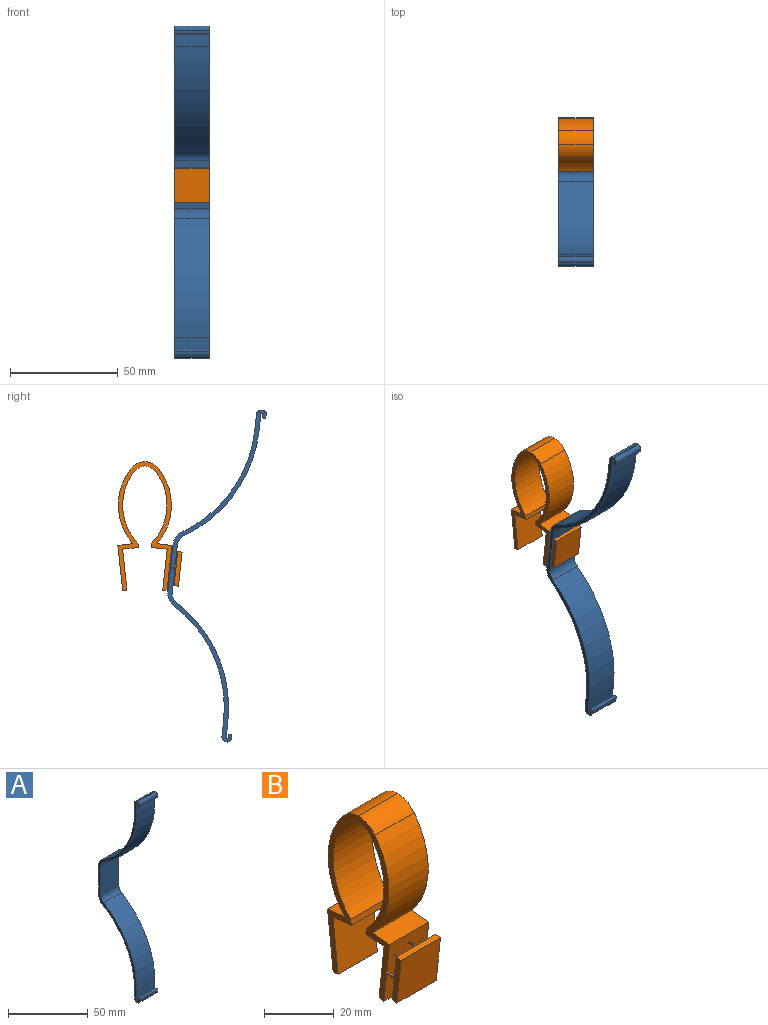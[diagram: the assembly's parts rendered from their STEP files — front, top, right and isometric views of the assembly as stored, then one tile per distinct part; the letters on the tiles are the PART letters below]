
ASSEMBLY  parts=2 mates=3
PART A: 31 faces, bbox 15.9x36.5x154.6 mm
  f0: plane 15.88x1.08mm, normal (0,1,0), area 17.2mm2, adj f9,f10,f15,f16
  f1: plane 15.88x7.55mm, normal (0,-1,0), area 119.8mm2, adj f2,f9,f10,f16
  f2: cylinder r=61.15mm len=52.35mm, axis (-1,0,0), area 997.7mm2, adj f1,f9,f10,f11
  f3: plane 22.18x15.88mm, normal (0,-1,0), area 349.4mm2, adj f9,f10,f11,f24,f30
  f4: plane 22.18x15.88mm, normal (0,1,0), area 349.3mm2, adj f9,f10,f14,f27,f30
  f5: cylinder r=59.15mm len=50.64mm, axis (-1,0,0), area 965mm2, adj f6,f9,f10,f14
  f6: plane 15.88x7.24mm, normal (0,1,0), area 114.9mm2, adj f5,f9,f10,f13
  f7: plane 15.88x0.39mm, normal (0,0,1), area 6.1mm2, adj f9,f10,f12,f13
  f8: plane 15.88x1.28mm, normal (0,-1,0), area 20.4mm2, adj f9,f10,f12,f15
  f9: plane 154.64x36.46mm, normal (1,0,0), area 365.1mm2, adj f0,f1,f2,f3,f4,f5,f6,f7
  f10: plane 154.64x36.46mm, normal (-1,0,0), area 365.1mm2, adj f0,f1,f2,f3,f4,f5,f6,f7
  f11: cylinder r=5.08mm len=15.88mm, axis (-1,0,0), area 82.9mm2, adj f2,f3,f9,f10
  f12: cylinder r=1.78mm len=15.88mm, axis (-1,0,0), area 44.3mm2, adj f7,f8,f9,f10
  f13: cylinder r=2.29mm len=15.88mm, axis (-1,0,0), area 57mm2, adj f6,f7,f9,f10
  f14: cylinder r=7.09mm len=15.88mm, axis (-1,0,0), area 115.6mm2, adj f4,f5,f9,f10
  f15: cylinder r=0.75mm len=15.88mm, axis (-1,0,0), area 37.4mm2, adj f0,f8,f9,f10
  f16: cylinder r=0.48mm len=15.88mm, axis (-1,0,0), area 23.8mm2, adj f0,f1,f9,f10
  f17: plane 15.88x1.08mm, normal (0,1,0), area 17.2mm2, adj f9,f10,f28,f29
  f18: plane 15.88x7.55mm, normal (0,-1,0), area 119.8mm2, adj f9,f10,f19,f29
  f19: cylinder r=61.15mm len=52.35mm, axis (-1,0,0), area 997.7mm2, adj f9,f10,f18,f24
  f20: cylinder r=59.15mm len=50.64mm, axis (-1,0,0), area 965mm2, adj f9,f10,f21,f27
  f21: plane 15.88x7.24mm, normal (0,1,0), area 114.9mm2, adj f9,f10,f20,f26
  f22: plane 15.88x0.39mm, normal (0,0,-1), area 6.1mm2, adj f9,f10,f25,f26
  f23: plane 15.88x1.28mm, normal (0,-1,0), area 20.4mm2, adj f9,f10,f25,f28
  f24: cylinder r=5.08mm len=15.88mm, axis (-1,0,0), area 82.9mm2, adj f3,f9,f10,f19
  f25: cylinder r=1.78mm len=15.88mm, axis (-1,0,0), area 44.3mm2, adj f9,f10,f22,f23
  f26: cylinder r=2.29mm len=15.88mm, axis (-1,0,0), area 57mm2, adj f9,f10,f21,f22
  f27: cylinder r=7.09mm len=15.88mm, axis (-1,0,0), area 115.6mm2, adj f4,f9,f10,f20
  f28: cylinder r=0.75mm len=15.88mm, axis (-1,0,0), area 37.4mm2, adj f9,f10,f17,f23
  f29: cylinder r=0.48mm len=15.88mm, axis (-1,0,0), area 23.8mm2, adj f9,f10,f17,f18
  f30: cylinder r=0.94mm len=2mm, axis (0,1,0), area 11.8mm2, adj f3,f4
PART B: 55 faces, bbox 15.9x29.7x59.8 mm
  f0: plane 15.88x15.78mm, normal (0,0.99,0.11), area 232.3mm2, adj f3,f5,f23,f24,f25,f27,f28,f29
  f1: plane 20.93x15.88mm, normal (0,-0.99,-0.11), area 314.4mm2, adj f2,f3,f5,f8,f23,f24,f25,f27
  f2: plane 15.88x1.99mm, normal (0,0.11,-0.99), area 31.8mm2, adj f1,f3,f5,f16
  f3: plane 59.8x29.74mm, normal (1,0,0), area 321.2mm2, adj f0,f1,f2,f4,f6,f7,f8,f9
  f4: plane 15.88x1.99mm, normal (0,-0.11,-0.99), area 31.8mm2, adj f3,f5,f11,f21
  f5: plane 59.8x29.74mm, normal (-1,0,0), area 321.2mm2, adj f0,f1,f2,f4,f6,f7,f8,f9
  f6: plane 15.88x6.88mm, normal (0,0.11,0.99), area 109.8mm2, adj f3,f5,f7,f11
  f7: cylinder r=27.38mm len=34.62mm, axis (1,0,0), area 595.2mm2, adj f3,f5,f6,f12
  f8: plane 15.88x6.88mm, normal (0,-0.11,0.99), area 109.8mm2, adj f1,f3,f5,f9
  f9: cylinder r=27.38mm len=34.62mm, axis (1,0,0), area 595.2mm2, adj f3,f5,f8,f10
  f10: cylinder r=9.08mm len=15.88mm, axis (1,0,0), area 122.1mm2, adj f3,f5,f9,f12
  f11: plane 20.93x15.88mm, normal (0,0.99,-0.11), area 334.2mm2, adj f3,f4,f5,f6
  f12: cylinder r=9.08mm len=15.88mm, axis (1,0,0), area 122.1mm2, adj f3,f5,f7,f10
  f13: cylinder r=25.38mm len=33.13mm, axis (1,0,0), area 574.1mm2, adj f3,f5,f14,f17
  f14: plane 15.88x1.99mm, normal (0,0.99,0.11), area 31.8mm2, adj f3,f5,f13,f15
  f15: plane 15.88x7.36mm, normal (0,0.11,-0.99), area 117.5mm2, adj f3,f5,f14,f16
  f16: plane 18.94x15.88mm, normal (0,0.99,0.11), area 302.4mm2, adj f2,f3,f5,f15
  f17: cylinder r=7.08mm len=15.88mm, axis (1,0,0), area 93.1mm2, adj f3,f5,f13,f22
  f18: cylinder r=25.38mm len=33.13mm, axis (1,0,0), area 574.1mm2, adj f3,f5,f19,f22
  f19: plane 15.88x1.99mm, normal (0,-0.99,0.11), area 31.8mm2, adj f3,f5,f18,f20
  f20: plane 15.88x7.36mm, normal (0,-0.11,-0.99), area 117.5mm2, adj f3,f5,f19,f21
  f21: plane 18.94x15.88mm, normal (0,-0.99,0.11), area 302.4mm2, adj f3,f4,f5,f20
  f22: cylinder r=7.08mm len=15.88mm, axis (1,0,0), area 93.1mm2, adj f3,f5,f17,f18
  f23: cylinder r=2.38mm len=5.06mm, axis (0,0.99,0.11), area 44.9mm2, adj f0,f1
  f24: plane 15.88x4.97mm, normal (0,-0.11,0.99), area 32.9mm2, adj f0,f1,f3,f5,f26,f41,f42
  f25: plane 15.88x4.97mm, normal (0,0.11,-0.99), area 33mm2, adj f0,f1,f3,f5,f26,f44,f45
  f26: plane 15.88x15.78mm, normal (0,-0.99,-0.11), area 252mm2, adj f3,f5,f24,f25
  f27: plane 2.98x0.6mm, normal (0,-0.11,0.99), area 1.8mm2, adj f0,f1,f3,f29
  f28: plane 2.98x0.6mm, normal (0,0.11,-0.99), area 1.8mm2, adj f0,f1,f3,f29
  f29: plane 3.03x0.72mm, normal (-1,0,0), area 1.2mm2, adj f0,f1,f27,f28
  f30: plane 2.98x0.6mm, normal (0,-0.11,0.99), area 1.8mm2, adj f0,f1,f5,f32
  f31: plane 2.98x0.6mm, normal (0,0.11,-0.99), area 1.8mm2, adj f0,f1,f5,f32
  f32: plane 3.03x0.72mm, normal (1,0,0), area 1.2mm2, adj f0,f1,f30,f31
  f33: plane 3.01x0.6mm, normal (0.71,-0.08,0.7), area 1.2mm2, adj f0,f1,f34,f35
  f34: plane 3.03x0.74mm, normal (-0.71,-0.08,0.7), area 1.8mm2, adj f0,f1,f33,f36
  f35: plane 3.03x0.74mm, normal (0.71,0.08,-0.7), area 1.8mm2, adj f0,f1,f33,f36
  f36: plane 3.01x0.6mm, normal (-0.71,0.08,-0.7), area 1.2mm2, adj f0,f1,f34,f35
  f37: plane 3.03x0.74mm, normal (-0.71,-0.08,0.7), area 1.8mm2, adj f0,f1,f38,f40
  f38: plane 3.01x0.6mm, normal (-0.71,0.08,-0.7), area 1.2mm2, adj f0,f1,f37,f39
  f39: plane 3.03x0.74mm, normal (0.71,0.08,-0.7), area 1.8mm2, adj f0,f1,f38,f40
  f40: plane 3.01x0.6mm, normal (0.71,-0.08,0.7), area 1.2mm2, adj f0,f1,f37,f39
  f41: plane 3.05x0.92mm, normal (-1,0,0), area 1.8mm2, adj f0,f1,f24,f43
  f42: plane 3.05x0.92mm, normal (1,0,0), area 1.8mm2, adj f0,f1,f24,f43
  f43: plane 2.98x0.4mm, normal (0,0.11,-0.99), area 1.2mm2, adj f0,f1,f41,f42
  f44: plane 3.05x0.92mm, normal (-1,0,0), area 1.8mm2, adj f0,f1,f25,f46
  f45: plane 3.05x0.92mm, normal (1,0,0), area 1.8mm2, adj f0,f1,f25,f46
  f46: plane 2.98x0.4mm, normal (0,-0.11,0.99), area 1.2mm2, adj f0,f1,f44,f45
  f47: plane 3.01x0.6mm, normal (-0.71,-0.08,0.7), area 1.2mm2, adj f0,f1,f48,f49
  f48: plane 3.03x0.74mm, normal (-0.71,0.08,-0.7), area 1.8mm2, adj f0,f1,f47,f50
  f49: plane 3.03x0.74mm, normal (0.71,-0.08,0.7), area 1.8mm2, adj f0,f1,f47,f50
  f50: plane 3.01x0.6mm, normal (0.71,0.08,-0.7), area 1.2mm2, adj f0,f1,f48,f49
  f51: plane 3.03x0.74mm, normal (-0.71,0.08,-0.7), area 1.8mm2, adj f0,f1,f52,f54
  f52: plane 3.01x0.6mm, normal (0.71,0.08,-0.7), area 1.2mm2, adj f0,f1,f51,f53
  f53: plane 3.03x0.74mm, normal (0.71,-0.08,0.7), area 1.8mm2, adj f0,f1,f52,f54
  f54: plane 3.01x0.6mm, normal (-0.71,-0.08,0.7), area 1.2mm2, adj f0,f1,f51,f53
PLACE A rot(axis=(1,0,0),6.1deg) t=(-1.29,-23.03,-9.62)mm
PLACE B t=(-1.29,-11.13,-0.34)mm fixed
MATE cylindrical A.f30 <-> B.f23  axis (0,0.99,0.11) through (-1.29,-24.02,-9.73)mm
MATE fastened B.f23 <-> A.f30  axis (0,-0.99,-0.11) through (-1.29,-22.53,-9.57)mm
MATE parallel A.f9 <-> B.f3  axis (1,0,0) through (6.65,-43.19,-11.78)mm
